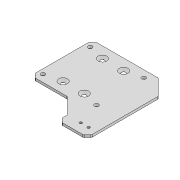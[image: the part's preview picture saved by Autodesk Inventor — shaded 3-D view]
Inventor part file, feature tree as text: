
AUTODESK INVENTOR PART (.ipt)
format: ipt  version: 2020 (Build 240168000, 168)  size: 172,032 bytes
history: native  units: mm
features: sketch x5, hole x3, extrude x2, chamfer x2, projected_geometry x2, other x1, fillet x1
ambient origin geometry x8: Origin, YZ Plane, XZ Plane, XY Plane, X Axis, Y Axis, Z Axis, Center Point
bodies: Body1 (feature_tree)
feature tree (16):
  other  "ソリッド1"
  extrude  "押し出し1"  Depth=80.0mm
  hole  "穴1"  [1 undecoded]
  hole  "穴2"  [1 undecoded]
  extrude  "押し出し2"  Depth=68.0mm
  hole  "穴3"  [1 undecoded]
  chamfer  "面取り1"  Distance=27.0mm
  chamfer  "面取り2"  Distance=50.0mm
  fillet  "フィレット3"  Radius=110.0mm
  sketch  "スケッチ1"
  sketch  "スケッチ2"
  sketch  "スケッチ3"
  sketch  "スケッチ4"
  projected_geometry  "投影ループ1"
  sketch  "スケッチ5"
  projected_geometry  "投影ループ2"
note: 3 required parameter values undecoded (feature->parameter linkage not recoverable at this tier; creation-order binding heuristic only, values carry confidence <= 0.55)
